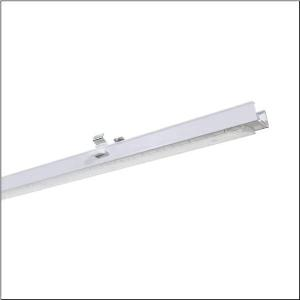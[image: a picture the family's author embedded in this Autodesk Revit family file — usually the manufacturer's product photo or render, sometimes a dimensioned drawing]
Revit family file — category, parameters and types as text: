
# Revit family: trunking_flex_31_51re14mb68b
name_source: partatom
category: Lighting Fixtures
units: mm (PartAtom-declared; Revit-internal decimal feet)

## family parameters
Cut with Voids When Loaded = No
Host = Face
Light Source = No
Part Type = Normal
Room Calculation Point = No
Round Connector Dimension = Use Diameter
Shared = No

## types (1)
- --- (1 x LED, 8000 lm, 50 W, 6500K)
    Apparent Load = 50 VA
    CIE Flux Codes = 72 92 98 99 100
    Color Rendering = 80
    Color Temperature = 6500K
    Default Elevation = 1800 mm
    Description = Trunking Flex 31, luminaire insert, of extruded aluminium section, coated, traffic white (RAL 9016), length: 1.472mm, width: 91mm, height: 53mm, LED rated luminous flux: 8.000lm, light colour: 865, control gear: ON/OFF Multilumen, with system connector: socket, mains connection: 220..240V, AC, 50/60Hz, rated input power: 50W, luminous flux adjustable on luminaire in four steps (4130/5610/6850/8000lm), connected load according to luminous flux setting (25/34/42/50W), primary light control with lens, of plastic, primary optical cover: cover, of PMMA, light emission: direct distribution, primary light characteristic: asymmetric, protection rating (complete): IP20, insulation class (complete): insulation class I (protective earthing), certification: CE, UKCA, impact resistance: IK02, permissible ambient temperature for indoor applications: -20..+40°C, packaging unit: 1 piece
    Height = 58 mm
    Lamp = 1 x LED
    Lamp Light Flux = 8000 lm
    Lamp Power = 50 W
    Lamp count = 1
    Length = 1472 mm
    Luminous efficacy = 160 lm/W
    Manufacturer = Siteco
    ModVariant = No
    Model = 51RE14MB68B
    Mounting Place = Ceiling
    Mounting Type = Pendant
    Number of Poles = 1
    OnlyDefault = Yes
    Power Factor = 1
    Product Name = Trunking Flex 31
    Product group = luminaire insert
    ProductGroupID = 901
    Protection Class = Protection class I
    Protection Degree = IP 20
    RLX_Detail_Level = 1
    RLX_Emergency_Light_Flux = 0 lm
    RLX_Emergency_Type = 0
    RLX_Emergency_Type_DB = No
    RlxData = <blob elided: 20985 chars, md5=445fb50d>
    Socket = socket
    Standby Power = 0 W
    System Light Flux = 8000 lm
    System Power = 50 W
    Type Comments = factory setting: luminous flux: 100 % | (ON | ON) | 300 mA
    Type Image = l_1266702.jpg
    URL = http://relux.com
    VarID = @adj_001359
    Voltage = 0 V
    Weight = 0.00 kg
    Width = 65 mm

## geometry (parser evidence)
native form markers: Blend x4, Sweep x10
no freeform markers — native parametric forms only
